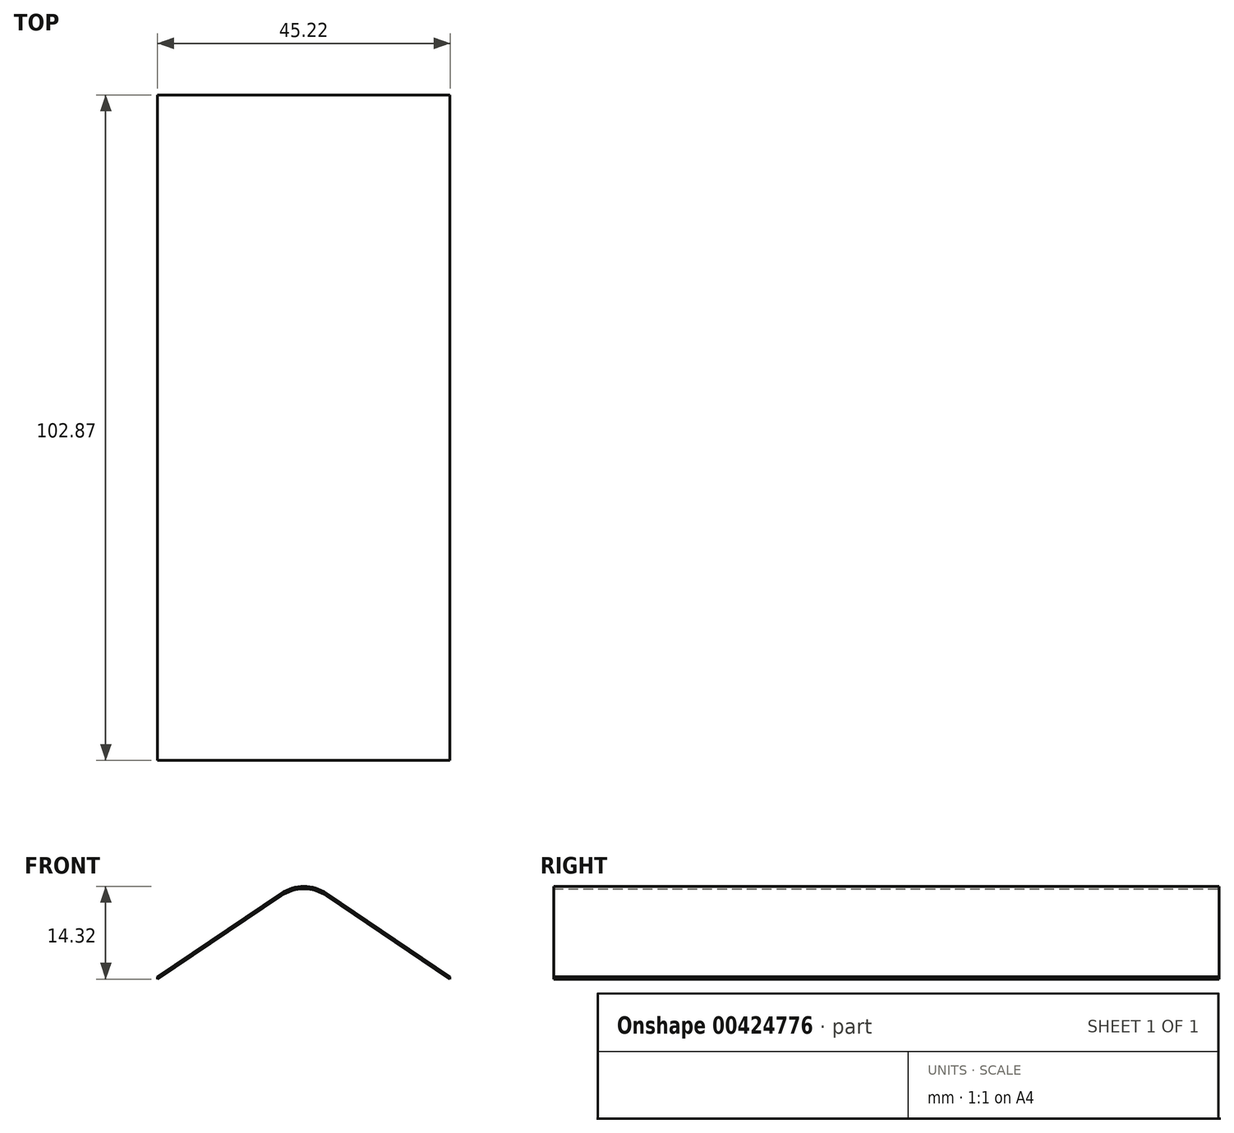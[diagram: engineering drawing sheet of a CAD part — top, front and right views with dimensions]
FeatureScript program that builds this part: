
annotation { "Feature Type Name" : "Feature", "Feature Type Description" : "" }
export const myFeature = defineFeature(function(context is Context, id is Id, definition is map)
    precondition{}
    {
        {
            var Q0;
            Q0=qCreatedBy(makeId("Front.planeOp"),FACE);
            var sketch = newSketch(context, id + "F0", { "sketchPlane" : qUnion([Q0])});
            skLineSegment(sketch, "E0", {"start": v(3.55, -0.7) * mm, "end": v(22.6, -13.56) * mm});
            skLineSegment(sketch, "E1", {"start": v(22.6, -13.94) * mm, "end": v(3.55, -1.09) * mm});
            skArc(sketch, "E2", {"start": v(3.55, -1.09) * mm, "mid": v(1.86, -0.28) * mm, "end": v(0, 0) * mm});
            skArc(sketch, "E3", {"start": v(3.55, -0.7) * mm, "mid": v(1.86, 0.1) * mm, "end": v(0, 0.38) * mm});
            skLineSegment(sketch, "E4", {"start": v(22.6, -13.56) * mm, "end": v(22.6, 11.08) * mm, "construction": true});
            skArc(sketch, "E5.MirrorCS", {"start": v(-3.55, -1.09) * mm, "mid": v(-1.86, -0.28) * mm, "end": v(0, 0) * mm});
            skArc(sketch, "E6.MirrorCS", {"start": v(-3.55, -0.7) * mm, "mid": v(-1.86, 0.1) * mm, "end": v(0, 0.38) * mm});
            skLineSegment(sketch, "E7.MirrorCS", {"start": v(-22.6, -13.94) * mm, "end": v(-3.55, -1.09) * mm});
            skLineSegment(sketch, "E8.MirrorCS", {"start": v(-3.55, -0.7) * mm, "end": v(-22.6, -13.56) * mm});
            skLineSegment(sketch, "E9.MirrorCS", {"start": v(-22.6, -13.56) * mm, "end": v(-22.6, -13.94) * mm});
            skLineSegment(sketch, "E10", {"start": v(22.6, -13.56) * mm, "end": v(22.6, -13.94) * mm});
            skSolve(sketch);
        }
        {
            var Q0;
            Q0 = qSketchRegion(id + "F0", true);
            extrude(context, id + "F1", {"entities" : qUnion([Q0]), "depth" : 102.87 * mm});
        }
    });
